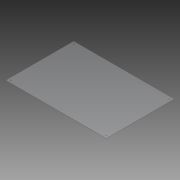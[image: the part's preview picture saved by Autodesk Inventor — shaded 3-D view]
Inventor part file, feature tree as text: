
AUTODESK INVENTOR PART (.ipt)
format: ipt  version: 2015 SP1 (Build 190203100, 203)  size: 101,376 bytes
history: native  units: in
note: dims shown in document units (in); Inventor stores cm internally (conversion verified against a paired STEP export)
features: extrude x1, sketch x1
ambient origin geometry x8: Origin, YZ Plane, XZ Plane, XY Plane, X Axis, Y Axis, Z Axis, Center Point
bodies: Body1 (feature_tree)
feature tree (2):
  extrude  "Extrusion3"  Depth=14.5in
  sketch  "Sketch1"  dims[d0=21.5in d1=14.5in d2=0.5in d3=0.5in d4=0.5in d5=0.5in d6=0.5in d7=0.5in d8=0.5in d9=0.5in d15=0.25in d16=0.25in d17=0.25in d19=0.25in d28=0.125in d29=0.0in]
